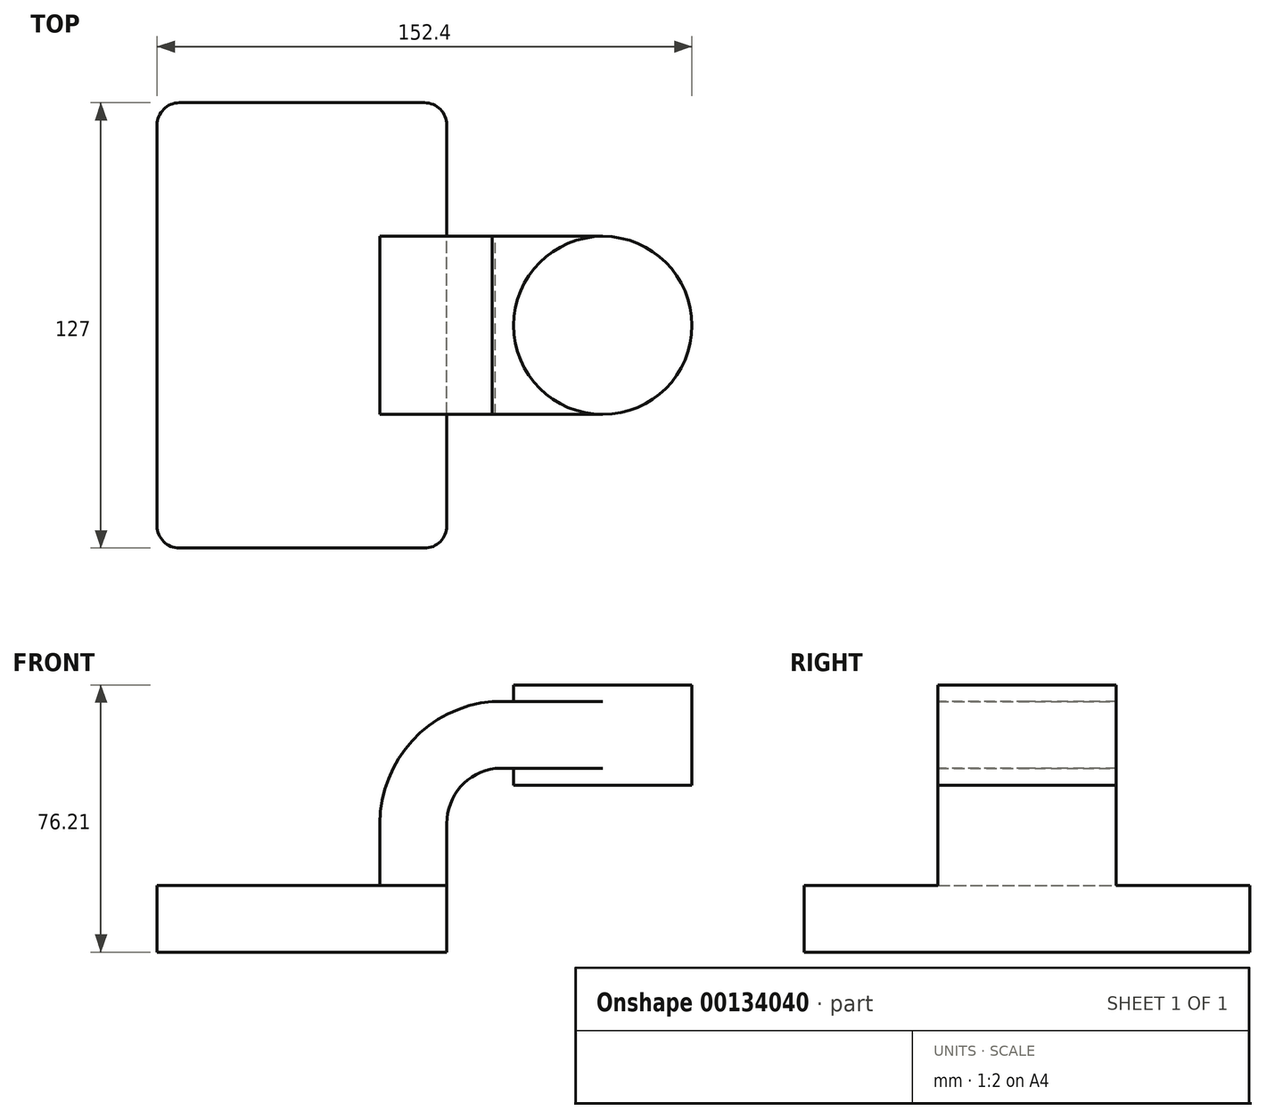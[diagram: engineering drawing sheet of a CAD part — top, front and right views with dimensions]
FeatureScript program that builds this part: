
annotation { "Feature Type Name" : "Feature", "Feature Type Description" : "" }
export const myFeature = defineFeature(function(context is Context, id is Id, definition is map)
    precondition{}
    {
        {
            var Q0;
            Q0=qCreatedBy(makeId("Front.planeOp"),FACE);
            var sketch = newSketch(context, id + "F0", { "sketchPlane" : qUnion([Q0])});
            skLineSegment(sketch, "E0.bottom", {"start": v(41.27, 9.53) * mm, "end": v(-41.28, 9.53) * mm});
            skLineSegment(sketch, "E0.top", {"start": v(41.28, -9.52) * mm, "end": v(-41.27, -9.53) * mm});
            skLineSegment(sketch, "E0.left", {"start": v(41.28, 9.53) * mm, "end": v(41.28, -9.52) * mm});
            skLineSegment(sketch, "E0.right", {"start": v(-41.28, 9.53) * mm, "end": v(-41.28, -9.53) * mm});
            skPoint(sketch, "E0.middle", {"position": v(0, 0) * mm});
            skLineSegment(sketch, "E1.bottom", {"start": v(111.12, 66.68) * mm, "end": v(60.32, 66.68) * mm});
            skLineSegment(sketch, "E1.top", {"start": v(111.12, 38.1) * mm, "end": v(60.32, 38.1) * mm});
            skLineSegment(sketch, "E1.left", {"start": v(111.12, 66.68) * mm, "end": v(111.12, 38.1) * mm});
            skLineSegment(sketch, "E1.right", {"start": v(60.32, 66.68) * mm, "end": v(60.32, 38.1) * mm});
            skPoint(sketch, "E1.middle", {"position": v(85.72, 52.39) * mm});
            skLineSegment(sketch, "E2", {"start": v(41.28, 9.53) * mm, "end": v(41.28, 27.13) * mm});
            skLineSegment(sketch, "E3", {"start": v(85.72, 38.1) * mm, "end": v(85.72, 66.68) * mm});
            skArc(sketch, "E4", {"start": v(41.28, 27.13) * mm, "mid": v(45.24, 37.62) * mm, "end": v(55.15, 42.88) * mm});
            skLineSegment(sketch, "E5", {"start": v(55.15, 42.88) * mm, "end": v(87.03, 42.88) * mm});
            skLineSegment(sketch, "E6.0", {"start": v(54.17, 61.93) * mm, "end": v(87.03, 61.93) * mm});
            skArc(sketch, "E6.1", {"start": v(22.23, 27.13) * mm, "mid": v(31.42, 50.75) * mm, "end": v(54.17, 61.93) * mm});
            skLineSegment(sketch, "E6.2", {"start": v(22.22, 9.53) * mm, "end": v(22.22, 27.13) * mm});
            skFitSpline(sketch, "E7", {"points": [v(-41.28, 9.52) * mm, v(54.17, 61.93) * mm], "startDerivative": vector(0, 54.43) * mm, "endDerivative": vector(140.65, 0) * mm});
            skSolve(sketch);
        }
        {
            var Q0;
            Q0=makeQuery(id+"F0.imprint","IMPRINT",FACE,{"disambiguationData":[TD([[makeQuery(id+"F0.imprint","IMPRINT",EDGE,{"derivedFrom":sQuery(id+"F0.wireOp",EDGE,"E0.top")}),-1.0]])]});
            extrude(context, id + "F1", {"entities" : qUnion([Q0]), "endBound" : BoundingType.SYMMETRIC, "depth" : 127 * mm});
        }
        {
            var Q0;
            {var subQ0=sQuery(id+"F0.wireOp",EDGE,"E2");Q0=makeQuery(id+"F0.imprint","IMPRINT",FACE,{"disambiguationData":[TD([[makeQuery(id+"F0.imprint","IMPRINT",EDGE,{"derivedFrom":subQ0}),1.0]])]});}
            var Q1;
            {var subQ0=sQuery(id+"F0.wireOp",EDGE,"E6.0");var subQ1=sQuery(id+"F0.wireOp",EDGE,"E1.right");var subQ2=makeQuery(id+"F0.imprint","INTERSECT",VERTEX,{"derivedFrom":[subQ1,subQ0]});Q1=makeQuery(id+"F0.imprint","IMPRINT",FACE,{"disambiguationData":[TD([[makeQuery(id+"F0.imprint","IMPRINT",EDGE,{"disambiguationData":[TD([[subQ2,-1.0]])],"derivedFrom":subQ1}),1.0]])]});}
            extrude(context, id + "F2", {"entities" : qUnion([Q0, Q1]), "operationType" : NewBodyOperationType.ADD, "endBound" : BoundingType.SYMMETRIC, "depth" : 50.8 * mm});
        }
        {
            var Q0;
            Q0=makeQuery(id+"F0.imprint","IMPRINT",FACE,{"disambiguationData":[TD([[makeQuery(id+"F0.imprint","IMPRINT",EDGE,{"derivedFrom":sQuery(id+"F0.wireOp",EDGE,"E6.1")}),1.0]])]});
            extrude(context, id + "F3", {"entities" : qUnion([Q0]), "operationType" : NewBodyOperationType.ADD, "endBound" : BoundingType.SYMMETRIC, "depth" : 15.88 * mm});
        }
        {
            var Q0;
            {var subQ4=sQuery(id+"F0.wireOp",EDGE,"E1.left");Q0=makeQuery(id+"F0.imprint","IMPRINT",FACE,{"disambiguationData":[TD([[makeQuery(id+"F0.imprint","IMPRINT",EDGE,{"derivedFrom":subQ4}),-1.0]])]});}
            var Q1;
            Q1=sQuery(id+"F0.wireOp",EDGE,"E3");
            revolve(context, id + "F4", {"operationType" : NewBodyOperationType.ADD, "entities" : qUnion([Q0]), "axis" : qUnion([Q1]), "revolveType" : RevolveType.FULL});
        }
        {
            var Q0;
            Q0=makeQuery(id+"F1.opExtrude","CAP_EDGE",EDGE,{"disambiguationData":[OSD([sQuery(id+"F0.wireOp",EDGE,"E0.left")])],"isStart":false});
            var Q1;
            Q1=makeQuery(id+"F1.opExtrude","CAP_EDGE",EDGE,{"disambiguationData":[OSD([sQuery(id+"F0.wireOp",EDGE,"E0.right")])],"isStart":false});
            var Q2;
            Q2=makeQuery(id+"F1.opExtrude","CAP_EDGE",EDGE,{"disambiguationData":[OSD([sQuery(id+"F0.wireOp",EDGE,"E0.left")])],"isStart":true});
            var Q3;
            Q3=makeQuery(id+"F1.opExtrude","CAP_EDGE",EDGE,{"disambiguationData":[OSD([sQuery(id+"F0.wireOp",EDGE,"E0.right")])],"isStart":true});
            fillet(context, id + "F5", {"entities" : qUnion([Q0, Q1, Q2, Q3]), "radius" : 6.35 * mm, "tangentPropagation" : true, "allowEdgeOverflow" : false});
        }
    });
